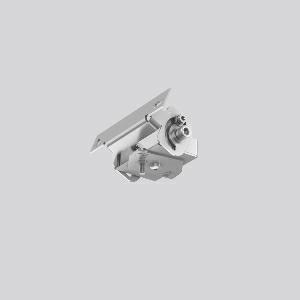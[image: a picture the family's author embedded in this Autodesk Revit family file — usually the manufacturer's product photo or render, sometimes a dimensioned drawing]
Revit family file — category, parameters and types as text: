
# Revit family: linedo_decke_wand_ausleger_982812_000_5280
name_source: partatom
category: Lighting Fixtures
units: mm (PartAtom-declared; Revit-internal decimal feet)

## family parameters
Cut with Voids When Loaded = No
Host = Face
Light Source = No
Part Type = Normal
Room Calculation Point = No
Round Connector Dimension = Use Diameter
Shared = No

## types (1)
- LINEDO Decke Wand Ausleger
    Apparent Load = 0 VA
    Default Elevation = 1800 mm
    Description = Ceiling/wall extension made of stainless steel. For 180°-pivotable horizontal installation of LINEDO luminaire modules, movable. 2 ceiling and wall brackets are required per luminaire module. With this accessory, the protection type of the luminaire module can be reduced to IP 20.
Colour: stainless steel
Length: 103 mm
Width: 47 mm
Height: 45 mm
Weight: 154 g
Type of Installation: Wall (surface)
    Height = 45 mm
    Lamp = 0 x
    Length = 103 mm
    Luminous efficacy = 0 lm/W
    Manufacturer = RZB
    ModVariant = No
    Model = 982812.000
    Mounting Place = Ceiling
    Mounting Type = Surface mounted
    Number of Poles = 1
    OnlyDefault = Yes
    Power Factor = 1
    Product Name = LINEDO Decke Wand Ausleger
    Product group = Surface mounted continuous line luminaire system
    ProductGroupID = 310
    Protection Class = Protection class
    Protection Degree = Degree of protection
    RLX_Detail_Level = 1
    RLX_Emergency_Light_Flux = 0 lm
    RLX_Emergency_Type = 0
    RLX_Emergency_Type_DB = No
    RlxData = <blob elided: 12625 chars, md5=92b32714>
    Standby Power = 0 W
    System Light Flux = 0 lm
    System Power = 0 W
    Type Comments = Product without accessories
    Type Image = 982812.000.jpg
    URL = http://relux.com
    VarID = ---
    Voltage = 0 V
    Weight = 0.00 kg
    Width = 47 mm

## geometry (parser evidence)
native form markers: Sweep x8
no freeform markers — native parametric forms only
